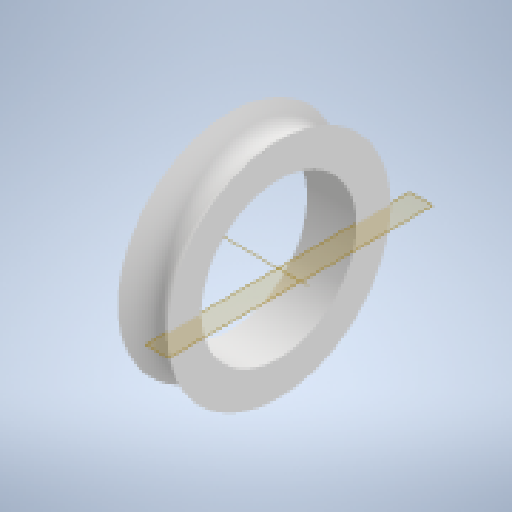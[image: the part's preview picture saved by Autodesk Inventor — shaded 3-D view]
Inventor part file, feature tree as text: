
AUTODESK INVENTOR PART (.ipt)
format: ipt  version: 2023 (Build 270158000, 158)  size: 180,224 bytes
history: native  units: mm
features: other x5, reference x2, plane x1, sketch x1, revolve x1
ambient origin geometry x8: Origin, YZ Plane, XZ Plane, XY Plane, X Axis, Y Axis, Z Axis, Center Point
bodies: Solid1 (feature_tree)
feature tree (10):
  plane  "Work Plane2"
  sketch  "Sketch1"  dims[d0=4.9mm d1=2.0mm d2=90.0deg]
  other  "Work Axis1"
  revolve  "Revolution1"  [1 undecoded]
  reference  "Reference1"
  reference  "Reference2"
  parser-record x1  (decoder bookkeeping rows leaked as tree rows — omitted from the tree; the rows remain in map.json)
  other  "Assembly1.iam"
  other  "bearing:1"
  other  "cord roller plate:1"
note: 1 file-system path scrubbed to <path> (originals preserved in map.json)
note: 1 required parameter value undecoded (feature->parameter linkage not recoverable at this tier; creation-order binding heuristic only, values carry confidence <= 0.55)
